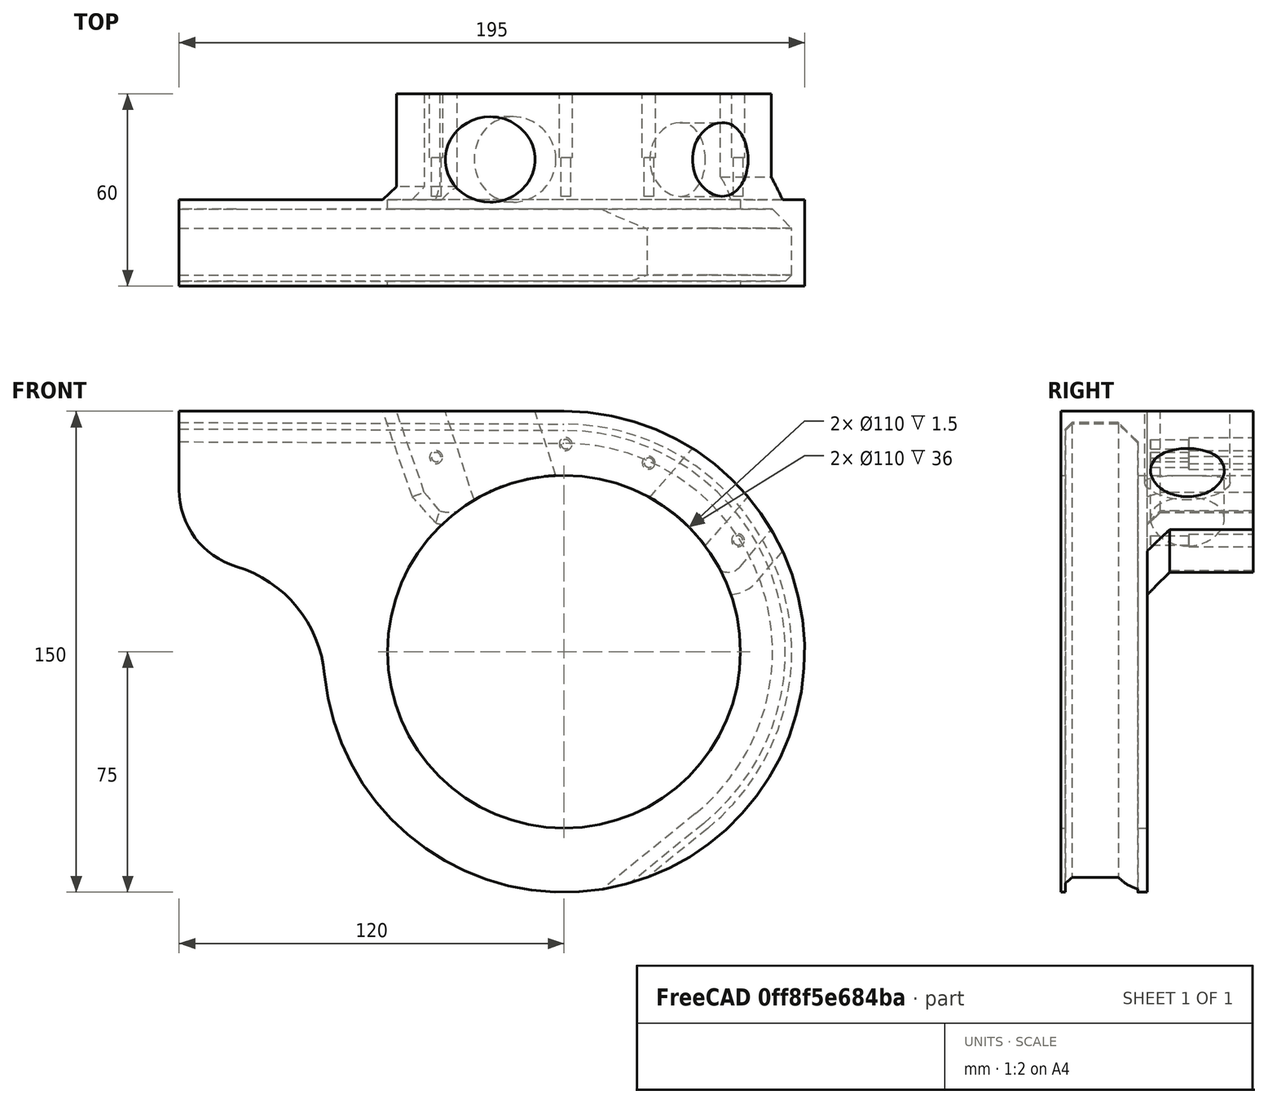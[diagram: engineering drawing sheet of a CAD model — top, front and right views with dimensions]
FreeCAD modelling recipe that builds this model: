
FCSTD DOCUMENT  (FreeCAD 0.19R)
Label: BottomWhiteBike7
License: All rights reserved
LicenseURL: http://en.wikipedia.org/wiki/All_rights_reserved
objects: Sketcher::SketchObject×9, PartDesign::Pocket×4, PartDesign::Chamfer×4, Part::Cylinder×2, PartDesign::Pad×1, Part::MultiFuse×1, PartDesign::Body×1, Part::Cut×1, Mesh::Feature×1
note: 32 computed .brp shape members not serialized (recipe doc carries the construction recipe); baked Part::Feature solids carry a one-line shape summary decoded from their .brp

FEATURE [Sketcher::SketchObject] Sketch
  FullyConstrained = false
  MapMode = 5
  Placement = pos=(0,0,0) rot=(1,0,0;1.5708rad)
  Support = -> [XZ_Plane]
  sketch-geometry (11):
    g0: LineSegment StartX=0 StartY=0 StartZ=0 EndX=112.706 EndY=65.0706 EndZ=0
    g1: LineSegment StartX=0 StartY=0 StartZ=0 EndX=7.3e-15 EndY=119.149 EndZ=0
    g2: LineSegment StartX=2.14e-14 StartY=70 StartZ=0 EndX=-199.884 EndY=70 EndZ=0
    g3: Circle CenterX=0 CenterY=0 CenterZ=0 NormalX=0 NormalY=0 NormalZ=1 AngleXU=0 Radius=45
    g4: ArcOfCircle CenterX=0 CenterY=0 CenterZ=0 NormalX=0 NormalY=0 NormalZ=1 AngleXU=0 Radius=70 StartAngle=3.5224 EndAngle=7.85398
    g5: LineSegment StartX=-120 StartY=75 StartZ=0 EndX=2.84e-14 EndY=75 EndZ=0
    g6: ArcOfCircle CenterX=0 CenterY=0 CenterZ=0 NormalX=0 NormalY=0 NormalZ=1 AngleXU=0 Radius=75 StartAngle=3.23571 EndAngle=7.85398
    g7: LineSegment StartX=-120 StartY=75 StartZ=0 EndX=-120 EndY=50.5061 EndZ=0
    g8: ArcOfCircle CenterX=-95 CenterY=50.5061 CenterZ=0 NormalX=0 NormalY=0 NormalZ=1 AngleXU=0 Radius=25 StartAngle=3.14159 EndAngle=4.4201
    g9: Circle CenterX=0 CenterY=0 CenterZ=0 NormalX=0 NormalY=0 NormalZ=1 AngleXU=0 Radius=55
    g10: ArcOfCircle CenterX=-113.419 CenterY=-10.7061 CenterZ=0 NormalX=0 NormalY=0 NormalZ=1 AngleXU=0 Radius=38.9235 StartAngle=0.0941155 EndAngle=1.27851
  constraints (25):
    c: Coincident(g0,g-1)
    c: Coincident(g1,g-1)
    c: Angle(g1) = 1.5708
    c: Angle(g0,g1) = 1.0472
    c: PointOnObject(g2,g1)
    c: Angle(g2) = 3.14159
    c: DistanceY(g2) = 70
    c: Coincident(g3,g-1)
    c: Coincident(g4,g-1)
    c: Diameter(g3) = 90
    c: Coincident(g4,g2)
    c: PointOnObject(g5,g1)
    c: Horizontal(g5)
    c: Coincident(g6,g-1)
    c: Coincident(g6,g5)
    c: Coincident(g5,g7)
    c: Vertical(g7)
    c: Tangent(g8,g7) = -1.5708
    c: Diameter(g6) = 150
    c: Distance(g5) = 120
    c: Diameter(g8) = 50
    c: Coincident(g9,g6)
    c: Diameter(g9) = 110
    c: Tangent(g10,g6) = 1.5708
    c: Tangent(g10,g8) = 1.5708
FEATURE [PartDesign::Pad] Pad
  Direction = (1,1,1)
  Length = 40
  Length2 = 20
  Placement = pos=(0,0,0) rot=(1,0,0;1.5708rad)
  Profile = -> Sketch
  Type = 4
FEATURE [Sketcher::SketchObject] Sketch001
  FullyConstrained = false
  MapMode = 5
  Placement = pos=(0,20,-4.4e-15) rot=(-1,0,0;1.5708rad)
  Support = -> [Pad]
  sketch-geometry (14):
    g0: GeomPoint X=0 Y=0 Z=0
    g1: LineSegment StartX=0 StartY=0 StartZ=0 EndX=101.779 EndY=-121.295 EndZ=0
    g2: LineSegment StartX=54.9288 StartY=-26.5684 StartZ=0 EndX=75.9423 EndY=-51.6114 EndZ=0
    g3: ArcOfCircle CenterX=0 CenterY=0 CenterZ=0 NormalX=0 NormalY=0 NormalZ=1 AngleXU=0 Radius=91.8204 StartAngle=5.68627 EndAngle=9.42478
    g4: LineSegment StartX=-211.759 StartY=-107.924 StartZ=0 EndX=-91.8204 EndY=2.84e-14 EndZ=0
    g5: LineSegment StartX=43.6212 StartY=-30.5051 StartZ=0 EndX=-31.6726 EndY=-44.3314 EndZ=0
    g6: LineSegment StartX=-42.2439 StartY=-45.8964 StartZ=0 EndX=-52.4011 EndY=-75.3951 EndZ=0
    g7: LineSegment StartX=0 StartY=0 StartZ=0 EndX=-69.9978 EndY=-203.289 EndZ=0
    g8: ArcOfCircle CenterX=51.1344 CenterY=-29.7522 CenterZ=0 NormalX=0 NormalY=0 NormalZ=1 AngleXU=0 Radius=4.95311 StartAngle=0.698132 EndAngle=2.38613
    g9: LineSegment StartX=47.5288 StartY=-26.3563 StartZ=0 EndX=43.6212 EndY=-30.5051 EndZ=0
    g10: LineSegment StartX=-52.4011 StartY=-75.3951 StartZ=0 EndX=-16.4761 EndY=-75.3951 EndZ=0
    g11: LineSegment StartX=-16.4761 StartY=-75.3951 StartZ=0 EndX=-30.9733 EndY=-107.924 EndZ=0
    g12: LineSegment StartX=-30.9733 StartY=-107.924 StartZ=0 EndX=-211.759 EndY=-107.924 EndZ=0
    g13: ArcOfCircle CenterX=-35.7204 CenterY=-53.4756 CenterZ=0 NormalX=0 NormalY=0 NormalZ=1 AngleXU=0 Radius=10 StartAngle=1.15406 EndAngle=2.28148
  constraints (24):
    c: Coincident(g1,g-1)
    c: Angle(g1,g-2) = 2.44346
    c: Coincident(g3,g-1)
    c: PointOnObject(g3,g-1)
    c: Coincident(g4,g3)
    c: Distance(g2,g1) = 25
    c: Parallel(g2,g1)
    c: Coincident(g7,g3)
    c: Angle(g7,g1) = 1.02974
    c: Parallel(g7,g6)
    c: Distance(g6,g7) = 25
    c: Tangent(g8,g2) = 1.5708
    c: Tangent(g9,g8) = -1.5708
    c: Coincident(g5,g9)
    c: Horizontal(g10)
    c: Coincident(g11,g10)
    c: Coincident(g12,g11)
    c: Coincident(g12,g4)
    c: Horizontal(g12)
    c: Coincident(g6,g13)
    c: Radius(g13) = 10
    c: Coincident(g13,g5)
    c: Coincident(g2,g3)
    c: Coincident(g10,g6)
FEATURE [PartDesign::Pocket] Pocket  label="FirstPocket-trim"
  BaseFeature = -> Pad
  Length = 33
  Length2 = 100
  Placement = pos=(0,0,0) rot=(1,0,0;1.5708rad)
  Profile = -> Sketch001
  Type = 0
FEATURE [Sketcher::SketchObject] Sketch003
  FullyConstrained = false
  MapMode = 5
  Placement = pos=(0,-13,1e-14) rot=(-1,0,0;1.5708rad)
  Support = -> [Pocket]
  sketch-geometry (5):
    g0: ArcOfCircle CenterX=0 CenterY=0 CenterZ=0 NormalX=0 NormalY=0 NormalZ=1 AngleXU=0 Radius=71 StartAngle=4.71239 EndAngle=7.17221
    g1: LineSegment StartX=-204.417 StartY=-71.8091 StartZ=0 EndX=0 EndY=-71 EndZ=0
    g2: LineSegment StartX=44.7421 StartY=55.1284 StartZ=0 EndX=-20.5649 EndY=108.132 EndZ=0
    g3: LineSegment StartX=-20.5649 StartY=108.132 StartZ=0 EndX=-158.302 EndY=56.4495 EndZ=0
    g4: LineSegment StartX=-158.302 StartY=56.4495 StartZ=0 EndX=-204.417 EndY=-71.8091 EndZ=0
  constraints (8):
    c: Coincident(g0,g-1)
    c: PointOnObject(g0,g-2)
    c: Diameter(g0) = 142
    c: Coincident(g1,g0)
    c: Tangent(g0,g2) = -1.5708
    c: Coincident(g2,g3)
    c: Coincident(g3,g4)
    c: Coincident(g4,g1)
FEATURE [PartDesign::Pocket] Pocket001  label="2ndPocket-thk"
  BaseFeature = -> Pocket
  Length = 25.5
  Length2 = -3
  Placement = pos=(0,0,0) rot=(1,0,0;1.5708rad)
  Profile = -> Sketch003
  Type = 4
FEATURE [Part::Cylinder] Cylinder  label="DT"
  Angle = 360
  AttacherType = Attacher::AttachEngine3D
  Height = 150
  Placement = pos=(1,-0.5,1) rot=(0,1,0;0.715585rad)
  Radius = 11.5
FEATURE [Part::Cylinder] Cylinder001  label="ST"
  Angle = 360
  AttacherType = Attacher::AttachEngine3D
  Height = 150
  Placement = pos=(1,-0.5,1) rot=(0,-1,0;0.314159rad)
  Radius = 13.3
FEATURE [Part::MultiFuse] Fusion
  Shapes = -> [Cylinder,Cylinder001]
FEATURE [Sketcher::SketchObject] Sketch004
  FullyConstrained = false
  MapMode = 5
  Placement = pos=(0,-38,4.2e-14) rot=(0,0.707107,0.707107;3.14159rad)
  sketch-geometry (11):
    g0: ArcOfCircle CenterX=0 CenterY=0 CenterZ=0 NormalX=0 NormalY=0 NormalZ=1 AngleXU=0 Radius=67.4561 StartAngle=1.5708 EndAngle=4.28769
    g1: LineSegment StartX=43.378 StartY=-56.1672 StartZ=0 EndX=97.643 EndY=-63.0707 EndZ=0
    g2: LineSegment StartX=97.643 StartY=-63.0707 StartZ=0 EndX=64.3329 EndY=-83.232 EndZ=0
    g3: LineSegment StartX=64.3329 StartY=-83.232 StartZ=0 EndX=-27.7948 EndY=-61.4636 EndZ=0
    g4: Circle CenterX=0 CenterY=0 CenterZ=0 NormalX=0 NormalY=0 NormalZ=1 AngleXU=0 Radius=57.041
    g5: LineSegment StartX=4.1e-15 StartY=67.4561 StartZ=0 EndX=181.167 EndY=67.4561 EndZ=0
    g6: ArcOfCircle CenterX=0 CenterY=0 CenterZ=0 NormalX=0 NormalY=0 NormalZ=1 AngleXU=0 Radius=67.5078 StartAngle=5.39067 EndAngle=6.9075
    g7: LineSegment StartX=56.6391 StartY=43.0635 StartZ=0 EndX=192.151 EndY=41.8244 EndZ=0
    g8: LineSegment StartX=192.151 StartY=41.8244 StartZ=0 EndX=181.167 EndY=67.4561 EndZ=0
    g9: ArcOfCircle CenterX=56.6183 CenterY=40.7899 CenterZ=0 NormalX=0 NormalY=0 NormalZ=1 AngleXU=0 Radius=2.27364 StartAngle=1.56165 EndAngle=3.7659
    g10: ArcOfCircle CenterX=43.6348 CenterY=-54.1491 CenterZ=0 NormalX=0 NormalY=0 NormalZ=1 AngleXU=0 Radius=2.03437 StartAngle=2.24908 EndAngle=4.58585
  constraints (15):
    c: Coincident(g0,g-1)
    c: Coincident(g2,g1)
    c: Coincident(g3,g2)
    c: Coincident(g3,g0)
    c: Coincident(g4,g0)
    c: PointOnObject(g0,g-2)
    c: Coincident(g5,g0)
    c: Horizontal(g5)
    c: Coincident(g6,g0)
    c: Coincident(g7,g8)
    c: Coincident(g8,g5)
    c: Tangent(g6,g9) = 1.5708
    c: Tangent(g7,g9) = 1.5708
    c: Tangent(g1,g10) = -1.5708
    c: Tangent(g6,g10) = 1.5708
FEATURE [Sketcher::SketchObject] Sketch006
  FullyConstrained = false
  MapMode = 5
  Placement = pos=(0,20,-1.8e-14) rot=(-1,0,0;1.5708rad)
  sketch-geometry (4):
    g0: Circle CenterX=-39.8919 CenterY=-60.6956 CenterZ=0 NormalX=0 NormalY=0 NormalZ=1 AngleXU=0 Radius=1.45
    g1: Circle CenterX=0.518637 CenterY=-64.7366 CenterZ=0 NormalX=0 NormalY=0 NormalZ=1 AngleXU=0 Radius=1.45
    g2: Circle CenterX=26.4007 CenterY=-58.9637 CenterZ=0 NormalX=0 NormalY=0 NormalZ=1 AngleXU=0 Radius=1.45
    g3: Circle CenterX=54.207 CenterY=-34.7174 CenterZ=0 NormalX=0 NormalY=0 NormalZ=1 AngleXU=0 Radius=1.45
  constraints (4):
    c: Diameter(g0) = 2.9
    c: Equal(g0,g1)
    c: Equal(g0,g2)
    c: Equal(g0,g3)
FEATURE [Sketcher::SketchObject] Sketch007
  FullyConstrained = false
  MapMode = 5
  Placement = pos=(0,20,-1.99e-14) rot=(-1,0,0;1.5708rad)
  sketch-geometry (4):
    g0: Circle CenterX=-39.9046 CenterY=-60.6617 CenterZ=0 NormalX=0 NormalY=0 NormalZ=1 AngleXU=0 Radius=2
    g1: Circle CenterX=0.50043 CenterY=-64.7556 CenterZ=0 NormalX=0 NormalY=0 NormalZ=1 AngleXU=0 Radius=2
    g2: Circle CenterX=26.3703 CenterY=-58.9325 CenterZ=0 NormalX=0 NormalY=0 NormalZ=1 AngleXU=0 Radius=2
    g3: Circle CenterX=54.2248 CenterY=-34.7424 CenterZ=0 NormalX=0 NormalY=0 NormalZ=1 AngleXU=0 Radius=2
  constraints (4):
    c: Diameter(g0) = 4
    c: Equal(g0,g1)
    c: Equal(g0,g2)
    c: Equal(g0,g3)
FEATURE [Sketcher::SketchObject] Sketch010
  FullyConstrained = false
  MapMode = 5
  Placement = pos=(-120,0,0) rot=(0.707107,0,-0.707107;3.14159rad)
  sketch-geometry (3):
    g0: LineSegment StartX=-75.6145 StartY=37.995 StartZ=0 EndX=-73.0073 EndY=40.6023 EndZ=0
    g1: LineSegment StartX=-73.0073 StartY=40.6023 StartZ=0 EndX=-81.082 EndY=45.6871 EndZ=0
    g2: LineSegment StartX=-81.082 StartY=45.6871 StartZ=0 EndX=-75.6145 EndY=37.995 EndZ=0
  constraints (4):
    c: Coincident(g0,g1)
    c: Coincident(g1,g2)
    c: Coincident(g0,g2)
    c: Angle(g0) = 0.785398
FEATURE [Sketcher::SketchObject] Sketch011
  FullyConstrained = false
  MapMode = 5
  Placement = pos=(0,0,0) rot=(0.57735,0.57735,0.57735;2.0944rad)
  Support = -> [YZ_Plane]
  sketch-geometry (3):
    g0: LineSegment StartX=-36.3196 StartY=77.3765 StartZ=0 EndX=-63.9469 EndY=104.18 EndZ=0
    g1: LineSegment StartX=-63.9469 StartY=104.18 StartZ=0 EndX=-42.5651 EndY=71.1309 EndZ=0
    g2: LineSegment StartX=-42.5651 StartY=71.1309 StartZ=0 EndX=-36.3196 EndY=77.3765 EndZ=0
  constraints (4):
    c: Coincident(g0,g1)
    c: Coincident(g2,g1)
    c: Coincident(g2,g0)
    c: Angle(g2) = 0.785398
FEATURE [Sketcher::SketchObject] Sketch012
  FullyConstrained = false
  MapMode = 5
  Placement = pos=(0,-38.5,5.12e-14) rot=(-1,0,0;1.5708rad)
  sketch-geometry (47):
    g0-g23: Circle x24 (B-spline internal-alignment scaffolding for g24; pole/knot coordinates omitted)
    g24: BSplineCurve PolesCount=24 KnotsCount=22 Degree=3 IsPeriodic=0
    g25-g46: GeomPoint x22 (B-spline internal-alignment scaffolding for g24; pole/knot coordinates omitted)
  constraints (5):
    c: Weight(g0) = 1
    c: Equal(g0, g1-g23) x23
    c: Coincident(g23,g0)
    c: InternalAlignment(g0-g23 -> g24) x24
    c: InternalAlignment(g25-g46 -> g24) x22
FEATURE [PartDesign::Chamfer] Chamfer
  Angle = 45
  Base = -> Pocket001 [Edge16]
  BaseFeature = -> Pocket001
  ChamferType = 0
  FlipDirection = false
  Placement = pos=(0,0,0) rot=(1,0,0;1.5708rad)
  Size = 7
  Size2 = 1
  SupportTransform = false
FEATURE [PartDesign::Chamfer] Chamfer001
  Angle = 45
  Base = -> Chamfer [Edge23,Edge5,Edge7]
  BaseFeature = -> Chamfer
  ChamferType = 0
  FlipDirection = false
  Placement = pos=(0,0,0) rot=(1,0,0;1.5708rad)
  Size = 4
  Size2 = 1
  SupportTransform = false
FEATURE [PartDesign::Chamfer] Chamfer002
  Angle = 45
  Base = -> Chamfer001 [Edge61]
  BaseFeature = -> Chamfer001
  ChamferType = 0
  FlipDirection = false
  Placement = pos=(0,0,0) rot=(1,0,0;1.5708rad)
  Size = 6
  Size2 = 1
  SupportTransform = false
FEATURE [PartDesign::Chamfer] Chamfer003
  Angle = 45
  Base = -> Chamfer002 [Edge36]
  BaseFeature = -> Chamfer002
  ChamferType = 0
  FlipDirection = false
  Placement = pos=(0,0,0) rot=(1,0,0;1.5708rad)
  Size = 2
  Size2 = 1
  SupportTransform = false
FEATURE [PartDesign::Pocket] Pocket002
  BaseFeature = -> Chamfer003
  Length = 32
  Length2 = 100
  Placement = pos=(0,0,0) rot=(1,0,0;1.5708rad)
  Profile = -> Sketch006
  Type = 0
FEATURE [PartDesign::Pocket] Pocket003
  BaseFeature = -> Pocket002
  Length = 20
  Length2 = 100
  Placement = pos=(0,0,0) rot=(1,0,0;1.5708rad)
  Profile = -> Sketch007
  Type = 0
FEATURE [PartDesign::Body] Body
  Group = -> [Sketch,Pad,Sketch001,Pocket,Sketch003,Pocket001,Sketch004,Sketch006,Sketch007,Sketch010,Sketch011,Sketch012,Chamfer,Chamfer001,Chamfer002,Chamfer003,Pocket002,Pocket003]
  Origin = -> Origin
  Tip = -> Pocket003
FEATURE [Part::Cut] Cut
  Base = -> Pocket003
  Tool = -> Fusion
FEATURE [Mesh::Feature] Mesh  label="Cut (Meshed)"
